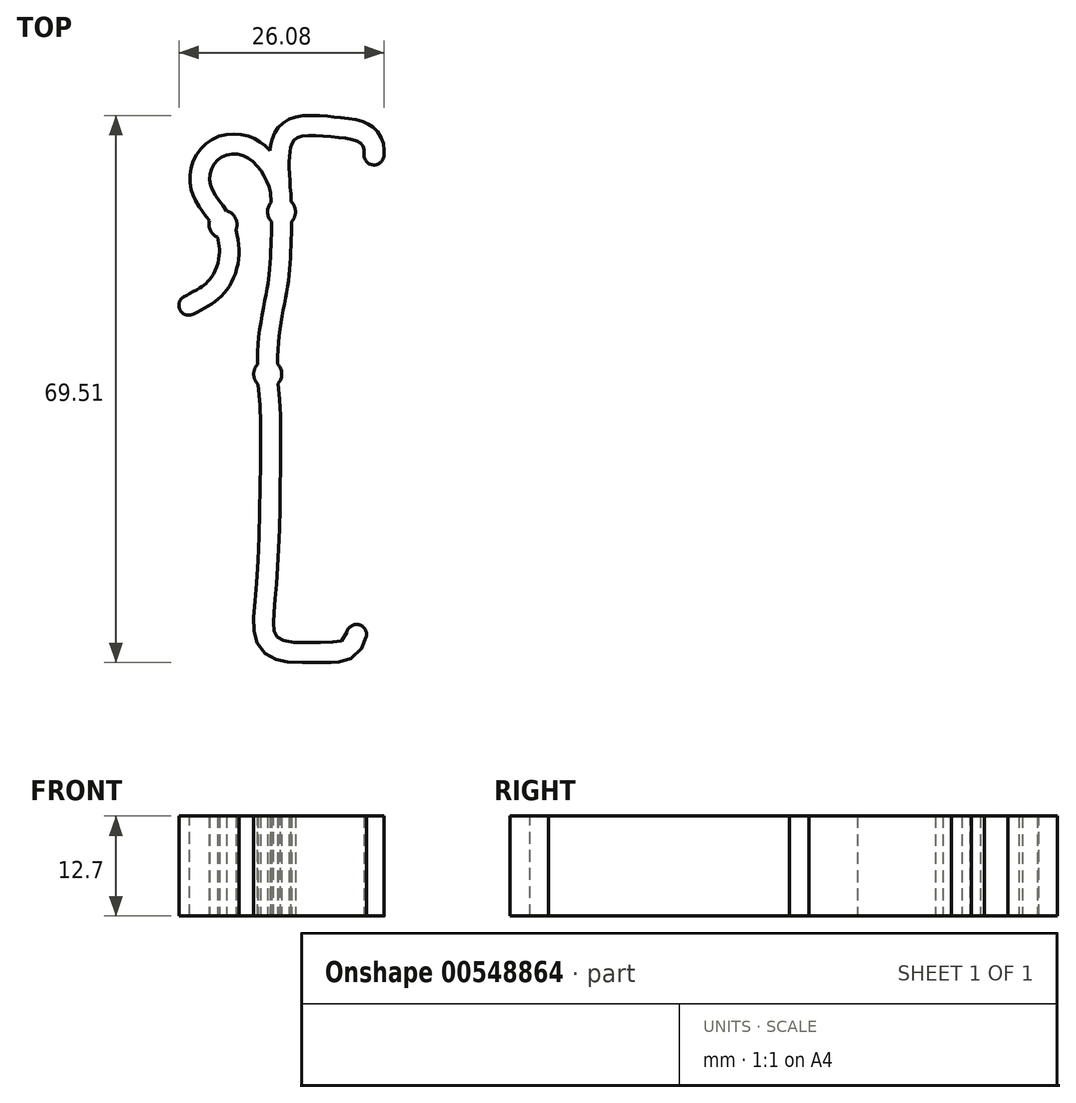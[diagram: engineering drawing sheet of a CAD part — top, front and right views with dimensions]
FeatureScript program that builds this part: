
annotation { "Feature Type Name" : "Feature", "Feature Type Description" : "" }
export const myFeature = defineFeature(function(context is Context, id is Id, definition is map)
    precondition{}
    {
        {
            var Q0;
            Q0=qCreatedBy(makeId("Top.planeOp"),FACE);
            var sketch = newSketch(context, id + "F0", { "sketchPlane" : qUnion([Q0])});
            skFitSpline(sketch, "E0", {"points": [v(8.33, -1.98) * mm, v(7.9, -0.53) * mm, v(4.31, 0.24) * mm, v(-0.2, 0.1) * mm, v(-1, -1.24) * mm, v(-1.15, -4.05) * mm, v(-0.87, -9.36) * mm, v(-0.95, -13.94) * mm, v(-1.27, -18.14) * mm, v(-2.03, -22.36) * mm, v(-2.66, -28) * mm, v(-2.33, -34.31) * mm, v(-2.28, -41.23) * mm, v(-2.47, -51.1) * mm, v(-2.93, -58.26) * mm, v(-3.15, -61.68) * mm, v(-2.92, -62.97) * mm, v(-2.12, -63.7) * mm, v(0.98, -64.01) * mm, v(4.76, -63.92) * mm, v(6.17, -62.63) * mm], "startDerivative": vector(4.3, 64.6) * mm, "endDerivative": vector(28.55, 101.03) * mm});
            skFitSpline(sketch, "E1.0", {"points": [v(10.87, -2.14) * mm, v(10.88, -1.9) * mm, v(10.9, -1.54) * mm, v(10.85, -0.95) * mm, v(10.75, -0.47) * mm, v(10.58, 0.05) * mm, v(10.3, 0.58) * mm, v(9.92, 1.07) * mm, v(9.55, 1.41) * mm, v(9.25, 1.63) * mm, v(8.95, 1.82) * mm, v(8.59, 2) * mm, v(8.18, 2.17) * mm, v(7.65, 2.33) * mm, v(7.01, 2.47) * mm, v(6.25, 2.6) * mm, v(5.5, 2.68) * mm, v(4.87, 2.74) * mm, v(4.37, 2.8) * mm, v(3.85, 2.84) * mm, v(3.18, 2.9) * mm, v(2.36, 2.94) * mm, v(1.52, 2.96) * mm, v(0.68, 2.92) * mm, v(-0.06, 2.82) * mm, v(-0.68, 2.66) * mm, v(-1.18, 2.47) * mm, v(-1.72, 2.18) * mm, v(-2.2, 1.81) * mm, v(-2.6, 1.39) * mm, v(-2.9, 0.94) * mm, v(-3.13, 0.5) * mm, v(-3.34, -0.05) * mm, v(-3.46, -0.51) * mm, v(-3.53, -0.9) * mm, v(-3.58, -1.2) * mm, v(-3.61, -1.49) * mm, v(-3.65, -1.88) * mm, v(-3.69, -2.39) * mm, v(-3.7, -3) * mm, v(-3.7, -3.85) * mm, v(-3.65, -4.98) * mm, v(-3.57, -6.4) * mm, v(-3.47, -7.87) * mm, v(-3.42, -9.04) * mm, v(-3.4, -9.91) * mm, v(-3.4, -10.77) * mm, v(-3.4, -11.8) * mm, v(-3.45, -12.83) * mm, v(-3.48, -13.67) * mm, v(-3.52, -14.5) * mm, v(-3.57, -15.53) * mm, v(-3.64, -16.52) * mm, v(-3.72, -17.29) * mm, v(-3.79, -17.84) * mm, v(-3.87, -18.4) * mm, v(-4, -19.15) * mm, v(-4.18, -20.13) * mm, v(-4.44, -21.4) * mm, v(-4.7, -22.8) * mm, v(-4.92, -24.31) * mm, v(-5.1, -25.9) * mm, v(-5.19, -27.28) * mm, v(-5.2, -28.41) * mm, v(-5.19, -29.53) * mm, v(-5.12, -30.88) * mm, v(-5, -32.46) * mm, v(-4.9, -33.72) * mm, v(-4.85, -34.69) * mm, v(-4.81, -35.66) * mm, v(-4.79, -36.9) * mm, v(-4.79, -38.44) * mm, v(-4.8, -39.81) * mm, v(-4.82, -40.98) * mm, v(-4.83, -42.18) * mm, v(-4.85, -43.76) * mm, v(-4.88, -45.7) * mm, v(-4.9, -47.67) * mm, v(-4.96, -49.61) * mm, v(-5.02, -51.48) * mm, v(-5.11, -53.25) * mm, v(-5.21, -54.91) * mm, v(-5.33, -56.47) * mm, v(-5.43, -57.66) * mm, v(-5.5, -58.56) * mm, v(-5.58, -59.42) * mm, v(-5.65, -60.23) * mm, v(-5.69, -61) * mm, v(-5.7, -61.57) * mm, v(-5.68, -62.14) * mm, v(-5.62, -62.74) * mm, v(-5.5, -63.29) * mm, v(-5.35, -63.74) * mm, v(-5.2, -64.08) * mm, v(-5.01, -64.43) * mm, v(-4.7, -64.9) * mm, v(-4.27, -65.33) * mm, v(-3.78, -65.69) * mm, v(-3.4, -65.91) * mm, v(-2.98, -66.09) * mm, v(-2.6, -66.22) * mm, v(-2.22, -66.31) * mm, v(-1.75, -66.4) * mm, v(-1.17, -66.48) * mm, v(-0.48, -66.52) * mm, v(0.2, -66.54) * mm, v(0.88, -66.55) * mm, v(1.55, -66.55) * mm, v(2.22, -66.55) * mm, v(2.89, -66.54) * mm, v(3.53, -66.52) * mm, v(4.03, -66.5) * mm, v(4.4, -66.49) * mm, v(4.63, -66.47) * mm, v(4.8, -66.46) * mm, v(4.93, -66.46) * mm, v(5.07, -66.45) * mm, v(5.29, -66.43) * mm, v(5.63, -66.38) * mm, v(6.18, -66.25) * mm, v(6.81, -65.97) * mm, v(7.42, -65.51) * mm, v(7.9, -64.97) * mm, v(8.22, -64.41) * mm, v(8.45, -63.87) * mm, v(8.57, -63.5) * mm, v(8.62, -63.32) * mm]});
            skArc(sketch, "E2", {"start": v(8.33, -1.98) * mm, "mid": v(9.52, -3.33) * mm, "end": v(10.87, -2.14) * mm});
            skArc(sketch, "E3", {"start": v(8.62, -63.32) * mm, "mid": v(7.74, -61.75) * mm, "end": v(6.17, -62.63) * mm});
            skSolve(sketch);
        }
        {
            var Q0;
            Q0=qCreatedBy(makeId("Top.planeOp"),FACE);
            var sketch = newSketch(context, id + "F1", { "sketchPlane" : qUnion([Q0])});
            skFitSpline(sketch, "E4", {"points": [v(-3.44, -8.07) * mm, v(-4.37, -4.71) * mm, v(-6.53, -2.35) * mm, v(-9.22, -2.08) * mm, v(-11, -3.77) * mm, v(-11, -6.34) * mm, v(-9.04, -9.28) * mm, v(-7.56, -13.49) * mm, v(-8.29, -17.8) * mm, v(-10.5, -20.63) * mm, v(-13.32, -22.26) * mm], "startDerivative": vector(0.39, 41.88) * mm, "endDerivative": vector(-30.67, -16.96) * mm});
            skFitSpline(sketch, "E5.0", {"points": [v(-0.93, -8.09) * mm, v(-0.92, -7.51) * mm, v(-1, -6.41) * mm, v(-1.36, -5.18) * mm, v(-1.73, -4.32) * mm, v(-2.03, -3.74) * mm, v(-2.34, -3.2) * mm, v(-2.69, -2.65) * mm, v(-3.1, -2.1) * mm, v(-3.56, -1.54) * mm, v(-4.1, -1) * mm, v(-4.61, -0.59) * mm, v(-5.08, -0.28) * mm, v(-5.58, 0) * mm, v(-6.23, 0.28) * mm, v(-7.05, 0.5) * mm, v(-7.88, 0.6) * mm, v(-8.72, 0.6) * mm, v(-9.56, 0.46) * mm, v(-10.4, 0.18) * mm, v(-11.16, -0.22) * mm, v(-11.83, -0.72) * mm, v(-12.42, -1.31) * mm, v(-12.91, -1.97) * mm, v(-13.3, -2.71) * mm, v(-13.59, -3.5) * mm, v(-13.75, -4.3) * mm, v(-13.79, -5.12) * mm, v(-13.72, -5.93) * mm, v(-13.57, -6.6) * mm, v(-13.4, -7.12) * mm, v(-13.19, -7.64) * mm, v(-12.89, -8.2) * mm, v(-12.51, -8.78) * mm, v(-12.14, -9.29) * mm, v(-11.8, -9.74) * mm, v(-11.48, -10.15) * mm, v(-11.26, -10.47) * mm, v(-11.1, -10.71) * mm, v(-10.95, -10.96) * mm, v(-10.78, -11.28) * mm, v(-10.58, -11.7) * mm, v(-10.42, -12.12) * mm, v(-10.28, -12.55) * mm, v(-10.17, -12.98) * mm, v(-10.1, -13.42) * mm, v(-10.05, -13.84) * mm, v(-10.03, -14.27) * mm, v(-10.06, -14.85) * mm, v(-10.16, -15.57) * mm, v(-10.4, -16.4) * mm, v(-10.73, -17.11) * mm, v(-11.07, -17.65) * mm, v(-11.38, -18.02) * mm, v(-11.62, -18.28) * mm, v(-11.87, -18.51) * mm, v(-12.11, -18.71) * mm, v(-12.4, -18.9) * mm, v(-12.83, -19.17) * mm, v(-13.5, -19.52) * mm, v(-14.17, -19.87) * mm, v(-14.53, -20.07) * mm]});
            skArc(sketch, "E6", {"start": v(-14.53, -20.07) * mm, "mid": v(-15.02, -21.77) * mm, "end": v(-13.32, -22.26) * mm});
            skArc(sketch, "E7", {"start": v(-3.44, -8.07) * mm, "mid": v(-2.09, -11.06) * mm, "end": v(-0.93, -7.98) * mm});
            skLineSegment(sketch, "E8", {"start": v(-3.41, -9.28) * mm, "end": v(-0.87, -9.28) * mm, "construction": true});
            skSolve(sketch);
        }
        {
            var Q0;
            Q0=qCreatedBy(makeId("Top.planeOp"),FACE);
            var sketch = newSketch(context, id + "F2", { "sketchPlane" : qUnion([Q0])});
            skCircle(sketch, "E9", {"center": v(-9.58, -10.9) * mm, "radius": 1.78 * mm});
            skLineSegment(sketch, "E10", {"start": v(-10.72, -11.4) * mm, "end": v(-8.43, -10.37) * mm, "construction": true});
            skSolve(sketch);
        }
        {
            var Q0;
            Q0=qCreatedBy(makeId("Top.planeOp"),FACE);
            var sketch = newSketch(context, id + "F3", { "sketchPlane" : qUnion([Q0])});
            skLineSegment(sketch, "E11", {"start": v(-5.16, -29.9) * mm, "end": v(-2.62, -29.9) * mm, "construction": true});
            skCircle(sketch, "E12", {"center": v(-3.9, -29.9) * mm, "radius": 1.78 * mm});
            skSolve(sketch);
        }
        {
            var Q0;
            Q0 = qSketchRegion(id + "F0", true);
            extrude(context, id + "F4", {"entities" : qUnion([Q0]), "depth" : 12.7 * mm, "offsetDistance" : 25.4 * mm});
        }
        {
            var Q0;
            Q0 = qSketchRegion(id + "F1", true);
            var Q1;
            Q1=makeQuery(id+"F4.opExtrude","CAP_FACE",FACE,{"disambiguationData":[OSD([sQuery(id+"F0.wireOp",EDGE,"E0"),sQuery(id+"F0.wireOp",EDGE,"E1.0"),sQuery(id+"F0.wireOp",EDGE,"9DLTUS2j-ohy2-zBtO-JpFI-nEIHASmz09dB"),sQuery(id+"F0.wireOp",EDGE,"xs1D2mEi-rNIV-qmPI-knIu-IgvRfARQ174m")])],"isStart":false});
            extrude(context, id + "F5", {"entities" : qUnion([Q0]), "operationType" : NewBodyOperationType.ADD, "endBound" : BoundingType.UP_TO_SURFACE, "depth" : 25.4 * mm, "endBoundEntityFace" : qUnion([Q1]), "offsetDistance" : 25.4 * mm});
        }
        {
            var Q0;
            Q0 = qSketchRegion(id + "F2", true);
            var Q1;
            {var subQ0=sQuery(id+"F0.wireOp",EDGE,"E3");var subQ1=sQuery(id+"F0.wireOp",EDGE,"E2");var subQ2=sQuery(id+"F0.wireOp",EDGE,"E1.0");var subQ3=sQuery(id+"F0.wireOp",EDGE,"E0");Q1=makeQuery(id+"F5.boolean.opBoolean","MERGE",FACE,{"derivedFrom":[makeQuery(id+"F4.opExtrude","CAP_FACE",FACE,{"disambiguationData":[OSD([subQ3,subQ2,subQ1,subQ0])],"isStart":false}),makeQuery(id+"F5.opExtrude","CAP_FACE",FACE,{"disambiguationData":[OSD([subQ3,subQ2,subQ1,subQ0])],"isStart":false})]});}
            extrude(context, id + "F6", {"entities" : qUnion([Q0]), "operationType" : NewBodyOperationType.ADD, "endBound" : BoundingType.UP_TO_SURFACE, "depth" : 25.4 * mm, "endBoundEntityFace" : qUnion([Q1]), "offsetDistance" : 25.4 * mm});
        }
        {
            var Q0;
            Q0 = qSketchRegion(id + "F3", true);
            var Q1;
            {var subQ0=sQuery(id+"F0.wireOp",EDGE,"E3");var subQ1=sQuery(id+"F0.wireOp",EDGE,"E2");var subQ2=sQuery(id+"F0.wireOp",EDGE,"E1.0");var subQ3=sQuery(id+"F0.wireOp",EDGE,"E0");Q1=makeQuery(id+"F6.boolean.opBoolean","MERGE",FACE,{"derivedFrom":[makeQuery(id+"F5.boolean.opBoolean","MERGE",FACE,{"derivedFrom":[makeQuery(id+"F4.opExtrude","CAP_FACE",FACE,{"disambiguationData":[OSD([subQ3,subQ2,subQ1,subQ0])],"isStart":false}),makeQuery(id+"F5.opExtrude","CAP_FACE",FACE,{"disambiguationData":[OSD([subQ3,subQ2,subQ1,subQ0])],"isStart":false})]}),makeQuery(id+"F6.opExtrude","CAP_FACE",FACE,{"disambiguationData":[OSD([subQ3,subQ2,subQ1,subQ0])],"isStart":false})]});}
            extrude(context, id + "F7", {"entities" : qUnion([Q0]), "operationType" : NewBodyOperationType.ADD, "endBound" : BoundingType.UP_TO_SURFACE, "depth" : 25.4 * mm, "endBoundEntityFace" : qUnion([Q1]), "offsetDistance" : 25.4 * mm});
        }
    });
